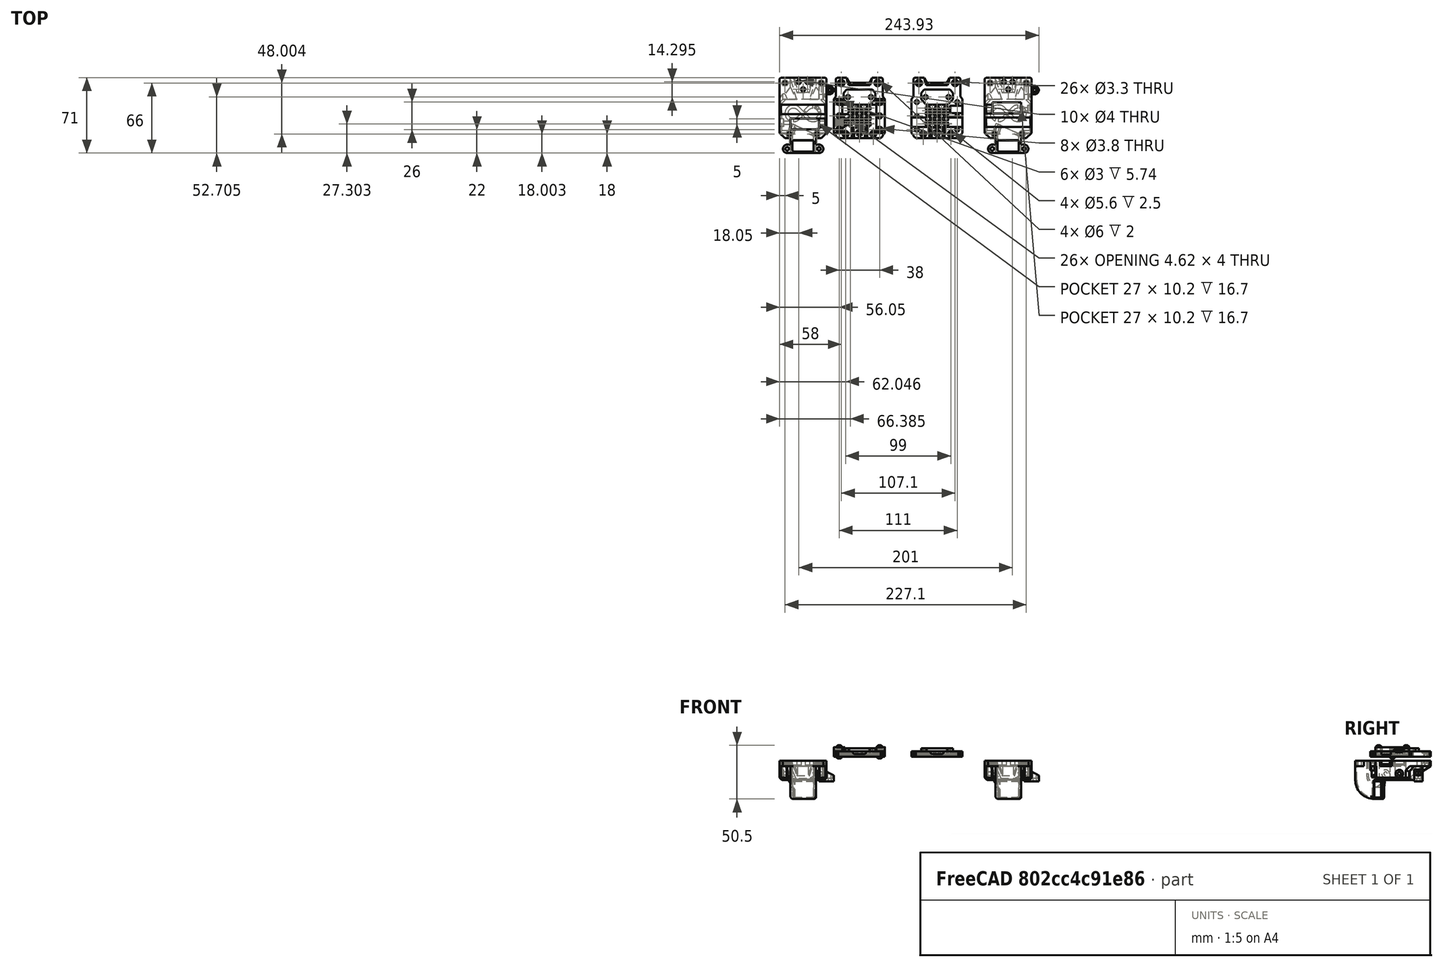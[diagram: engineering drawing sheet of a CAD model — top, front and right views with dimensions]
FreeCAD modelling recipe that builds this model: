
FCSTD DOCUMENT  (FreeCAD 0.19R24291 (Git))
Label: idex-tmp-assembly
License: All rights reserved
LicenseURL: http://en.wikipedia.org/wiki/All_rights_reserved
objects: Part::FeaturePython×12, Part::Feature×6, App::Part×1
note: 18 computed .brp shape members not serialized (recipe doc carries the construction recipe); baked Part::Feature solids carry a one-line shape summary decoded from their .brp

FEATURE [Part::Feature] Cut008004003012001003001010001023001  label="ex2-front"
  Placement = pos=(73,0,0) rot=(0,0,1;0rad)
  shape: bbox 48 x 57 x 8 mm, 204 faces (baked)
FEATURE [Part::Feature] Cut008004003012001003001010001024001  label="ex1-front"
  shape: bbox 48 x 57 x 8 mm, 204 faces (baked)
FEATURE [Part::Feature] Cut008004003012001003001010001026005  label="front-belt-clamp001"
  shape: bbox 10.5 x 32 x 4.5 mm, 49 faces (baked)
FEATURE [Part::Feature] Cut008004003012001003001010001026004001  label="fron-rf001"
  shape: bbox 8 x 32 x 4 mm, 18 faces (baked)
FEATURE [Part::Feature] Chamfer005021077002006007019003032007004001  label="ex1-back"
  Placement = pos=(-53,0,-6.5e-15) rot=(0,1,0;3.14159rad)
  shape: bbox 50.93 x 72.49 x 37.34 mm, 491 faces (baked)
FEATURE [Part::Feature] Chamfer005021077002006007019003032007005001  label="ex2-back"
  Placement = pos=(140,0,2.6e-14) rot=(0,1,0;3.14159rad)
  shape: bbox 50.93 x 72.49 x 37.34 mm, 487 faces (baked)
FEATURE [Part::FeaturePython] HeatSet  label="M3-HeatSet"  # WARN: FeaturePython — macro-defined, semantics opaque (R4)
  Placement = pos=(19,-13,0.5) rot=(-1,0,0;3.14159rad)
  baseObject = -> Cut008004003012001003001010001024001 [Edge142]
  diameter = 3
  invert = true
  leftHanded = false
  offset = 0
FEATURE [Part::FeaturePython] HeatSet001  label="M3-HeatSet001"  # WARN: FeaturePython — macro-defined, semantics opaque (R4)
  Placement = pos=(19,13,0.5) rot=(-1,0,0;3.14159rad)
  baseObject = -> Cut008004003012001003001010001024001 [Edge144]
  diameter = 3
  invert = true
  leftHanded = false
  offset = 0
FEATURE [Part::FeaturePython] HeatSet002  label="M3-HeatSet002"  # WARN: FeaturePython — macro-defined, semantics opaque (R4)
  Placement = pos=(-19,13,0.5) rot=(-1,0,0;3.14159rad)
  baseObject = -> Cut008004003012001003001010001024001 [Edge143]
  diameter = 3
  invert = true
  leftHanded = false
  offset = 0
FEATURE [Part::FeaturePython] HeatSet003  label="M3-HeatSet003"  # WARN: FeaturePython — macro-defined, semantics opaque (R4)
  Placement = pos=(-19,-13,0.5) rot=(-1,0,0;3.14159rad)
  baseObject = -> Cut008004003012001003001010001024001 [Edge145]
  diameter = 3
  invert = true
  leftHanded = false
  offset = 0
FEATURE [Part::FeaturePython] HeatSet004  label="M3-HeatSet004"  # WARN: FeaturePython — macro-defined, semantics opaque (R4)
  Placement = pos=(-19,0,9.5) rot=(0,0,1;0rad)
  baseObject = -> Cut008004003012001003001010001026005 [Edge20]
  diameter = 3
  invert = false
  leftHanded = false
  offset = 0
FEATURE [Part::FeaturePython] HeatSet005  label="M3-HeatSet005"  # WARN: FeaturePython — macro-defined, semantics opaque (R4)
  Placement = pos=(19,-2.3e-15,9.5) rot=(0,0,1;0rad)
  baseObject = -> Cut008004003012001003001010001026004001 [Edge12]
  diameter = 3
  invert = false
  leftHanded = false
  offset = 0
FEATURE [Part::FeaturePython] Screw  label="M3x8-Screw"  # Fasteners workbench fastener (typed FeaturePython)
  Placement = pos=(-19,13,9.5) rot=(0,0,1;0rad)
  baseObject = -> Cut008004003012001003001010001026005 [Edge19]
  diameter = 1
  invert = false
  leftHanded = false
  length = 1
  lengthCustom = 8
  matchOuter = false
  offset = 0
  thread = false
  type = 42
FEATURE [Part::FeaturePython] Screw001  label="M3x8-Screw001"  # Fasteners workbench fastener (typed FeaturePython)
  Placement = pos=(-19,-13,9.5) rot=(0,0,1;0rad)
  baseObject = -> Cut008004003012001003001010001026005 [Edge18]
  diameter = 1
  invert = false
  leftHanded = false
  length = 1
  lengthCustom = 8
  matchOuter = false
  offset = 0
  thread = false
  type = 42
FEATURE [Part::FeaturePython] Screw002  label="M3x8-Screw002"  # Fasteners workbench fastener (typed FeaturePython)
  Placement = pos=(19,13,9.5) rot=(0,0,1;0rad)
  baseObject = -> Cut008004003012001003001010001026004001 [Edge9]
  diameter = 1
  invert = false
  leftHanded = false
  length = 1
  lengthCustom = 8
  matchOuter = false
  offset = 0
  thread = false
  type = 42
FEATURE [Part::FeaturePython] Screw003  label="M3x8-Screw003"  # Fasteners workbench fastener (typed FeaturePython)
  Placement = pos=(19,-13,9.5) rot=(0,0,1;0rad)
  baseObject = -> Cut008004003012001003001010001026004001 [Edge10]
  diameter = 1
  invert = false
  leftHanded = false
  length = 1
  lengthCustom = 8
  matchOuter = false
  offset = 0
  thread = false
  type = 42
FEATURE [Part::FeaturePython] Screw004  label="M3x8-Screw006"  # Fasteners workbench fastener (typed FeaturePython)
  Placement = pos=(19,0,0.5) rot=(-1,0,0;3.14159rad)
  baseObject = -> Cut008004003012001003001010001024001 [Edge151]
  diameter = 1
  invert = true
  leftHanded = false
  length = 1
  lengthCustom = 8
  matchOuter = false
  offset = 0
  thread = false
  type = 42
FEATURE [Part::FeaturePython] Screw005  label="M3x8-Screw007"  # Fasteners workbench fastener (typed FeaturePython)
  Placement = pos=(-19,0,0.5) rot=(-1,0,0;3.14159rad)
  baseObject = -> Cut008004003012001003001010001024001 [Edge150]
  diameter = 1
  invert = true
  leftHanded = false
  length = 1
  lengthCustom = 8
  matchOuter = false
  offset = 0
  thread = false
  type = 42
FEATURE [App::Part] Part
  Group = -> [Cut008004003012001003001010001023001,Cut008004003012001003001010001024001,Cut008004003012001003001010001026005,Cut008004003012001003001010001026004001,Chamfer005021077002006007019003032007004001,Chamfer005021077002006007019003032007005001,HeatSet,HeatSet001,HeatSet002,HeatSet003,HeatSet004,HeatSet005,Screw,Screw001,Screw002,Screw003,Screw004,Screw005]
  Origin = -> Origin
